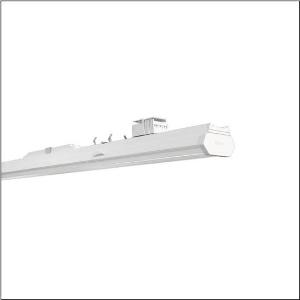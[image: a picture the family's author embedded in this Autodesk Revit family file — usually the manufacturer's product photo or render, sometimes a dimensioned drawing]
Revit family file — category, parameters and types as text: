
# Revit family: licross_r__11_protected_mo_51td11cn49xg_045e
name_source: partatom
category: Lighting Fixtures
units: mm (PartAtom-declared; Revit-internal decimal feet)

## family parameters
Cut with Voids When Loaded = No
Host = Face
Light Source = No
Part Type = Normal
Room Calculation Point = No
Round Connector Dimension = Use Diameter
Shared = No

## types (1)
- --- (1 x LED, 9030 lm, 49.4 W, 4000K)
    Apparent Load = 49 VA
    CIE Flux Codes = 83 94 98 100 100
    Color Rendering = 80
    Color Temperature = 4000K
    Default Elevation = 1800 mm
    Description = Licross® 11 Protected MO, luminaire insert, of sheet steel, galvanised, coil coated, white, length: 1.500mm, width: 90mm, height: 101mm, LED rated luminous flux: 9.030lm, light colour: 840, SDCM (Standard Deviation of Colour Matching)MacAdam ≤ 2 SDCM (initial), control gear: ON/OFF Multilumen, CLOi, with plug, 3-pole, with phase selection, mains connection: 220..240V, AC, 50/60Hz, start of lifetime: 49W, end of service life: 55W, internal wiring halogen-free, primary light control with lens, of plastic, primary optical cover: cover, of PMMA, light emission: direct distribution, primary light characteristic: symmetric, protection rating (complete): IP54, insulation class (complete): insulation class I (protective earthing), certification: CE, ENEC, VDE, UKCA, protection symbol: D if used in an environment with non-conductive dust loads with corresponding accessories, impact resistance: IK06, permissible ambient temperature for indoor applications: -35..+40°C, corresponds to IFS (International Featured Standards) requirements for safety and quality in the food industry, reducing of maximum allowable ambient temperature of 5°C with ceiling mounting, LABS conformity tested according to VDMA 24364:2018-05, packaging unit: 1 piece
    Height = 92 mm
    Lamp = 1 x LED
    Lamp Light Flux = 9030 lm
    Lamp Power = 49.4 W
    Lamp count = 1
    Length = 1500 mm
    Luminous efficacy = 183 lm/W
    Manufacturer = Siteco
    ModVariant = No
    Model = 51TD11CN49XG
    Mounting Place = Ceiling
    Mounting Type = Pendant
    Number of Poles = 1
    OnlyDefault = Yes
    Power Factor = 1
    Product Name = Licross® 11 Protected MO
    Product group = luminaire insert | ceiling pendant
    ProductGroupID = 901
    Protection Class = Protection class I
    Protection Degree = IP 54
    RLX_Detail_Level = 1
    RLX_Emergency_Light_Flux = 0 lm
    RLX_Emergency_Type = 0
    RLX_Emergency_Type_DB = No
    RlxData = <blob elided: 21997 chars, md5=b4790f09>
    Socket = socket
    Standby Power = 0 W
    System Light Flux = 9030 lm
    System Power = 49 W
    Type Comments = factory setting: luminous flux: 100 % | (A | C | E) | 113 mA
    Type Image = l_1256145.jpg
    URL = http://relux.com
    VarID = @adj_093479
    Voltage = 0 V
    Weight = 0.00 kg
    Width = 88 mm

## geometry (parser evidence)
native form markers: Blend x4, Sweep x12
no freeform markers — native parametric forms only
